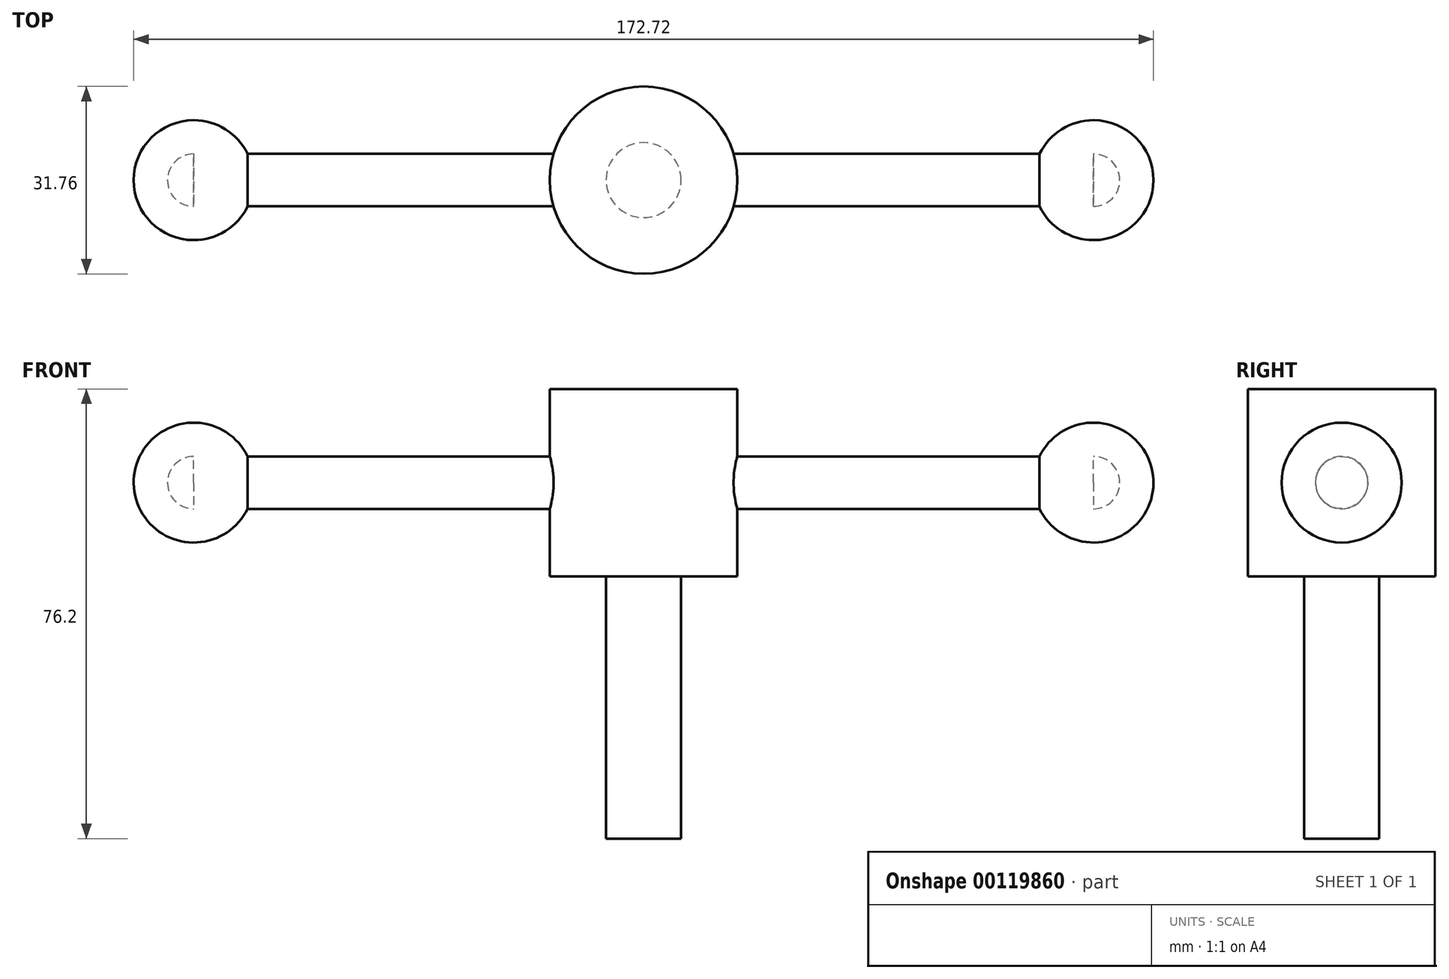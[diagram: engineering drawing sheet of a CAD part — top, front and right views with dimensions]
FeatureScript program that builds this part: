
annotation { "Feature Type Name" : "Feature", "Feature Type Description" : "" }
export const myFeature = defineFeature(function(context is Context, id is Id, definition is map)
    precondition{}
    {
        {
            var Q0;
            Q0=qCreatedBy(makeId("Top.planeOp"),FACE);
            var sketch = newSketch(context, id + "F0", { "sketchPlane" : qUnion([Q0])});
            skCircle(sketch, "E0", {"center": v(0, 0) * mm, "radius": 15.88 * mm});
            skCircle(sketch, "E1", {"center": v(0, 0) * mm, "radius": 6.35 * mm});
            skSolve(sketch);
        }
        {
            var Q0;
            Q0=makeQuery(id+"F0.imprint","IMPRINT",FACE,{"disambiguationData":[TD([[makeQuery(id+"F0.imprint","IMPRINT",EDGE,{"derivedFrom":sQuery(id+"F0.wireOp",EDGE,"E0")}),1.0]])]});
            extrude(context, id + "F1", {"entities" : qUnion([Q0]), "depth" : 31.75 * mm});
        }
        {
            var Q0;
            Q0=makeQuery(id+"F0.imprint","IMPRINT",FACE,{"disambiguationData":[TD([[makeQuery(id+"F0.imprint","IMPRINT",EDGE,{"derivedFrom":sQuery(id+"F0.wireOp",EDGE,"E1")}),1.0]])]});
            extrude(context, id + "F2", {"entities" : qUnion([Q0]), "operationType" : NewBodyOperationType.ADD, "depth" : 31.75 * mm, "hasSecondDirection" : true, "secondDirectionOppositeDirection" : true, "secondDirectionDepth" : 44.45 * mm});
        }
        {
            var Q0;
            Q0=qCreatedBy(makeId("Right.planeOp"),FACE);
            var sketch = newSketch(context, id + "F3", { "sketchPlane" : qUnion([Q0])});
            skLineSegment(sketch, "E2", {"start": v(0, 30.86) * mm, "end": v(0, 0) * mm, "construction": true});
            skLineSegment(sketch, "E3", {"start": v(0, 15.88) * mm, "end": v(-13.68, 15.88) * mm, "construction": true});
            skCircle(sketch, "E4", {"center": v(0, 15.88) * mm, "radius": 4.45 * mm});
            skSolve(sketch);
        }
        {
            var Q0;
            Q0 = qSketchRegion(id + "F3", true);
            extrude(context, id + "F4", {"entities" : qUnion([Q0]), "operationType" : NewBodyOperationType.ADD, "depth" : 76.2 * mm, "hasSecondDirection" : true, "secondDirectionOppositeDirection" : true, "secondDirectionDepth" : 76.2 * mm});
        }
        {
            var Q0;
            Q0=makeQuery(id+"F4.opExtrude","CAP_FACE",FACE,{"disambiguationData":[OSD([sQuery(id+"F3.wireOp",EDGE,"E4")])],"isStart":false});
            var sketch = newSketch(context, id + "F5", { "sketchPlane" : qUnion([Q0])});
            skCircle(sketch, "E5", {"center": v(0, 15.88) * mm, "radius": 10.16 * mm});
            skLineSegment(sketch, "E6", {"start": v(-10.16, 15.88) * mm, "end": v(10.16, 15.88) * mm});
            skSolve(sketch);
        }
        {
            var Q0;
            {var subQ0=sQuery(id+"F5.wireOp",EDGE,"E6");var subQ1=sQuery(id+"F5.wireOp",EDGE,"E5");var subQ2=makeQuery(id+"F5.imprint","INTERSECT",VERTEX,{"disambiguationData":[OD(0.0)],"derivedFrom":[subQ1,subQ0]});Q0=makeQuery(id+"F5.imprint","IMPRINT",FACE,{"disambiguationData":[TD([[makeQuery(id+"F5.imprint","IMPRINT",EDGE,{"disambiguationData":[TD([[subQ2,-1.0]])],"derivedFrom":subQ1}),1.0]])]});}
            var Q1;
            {var subQ0=sQuery(id+"F5.wireOp",EDGE,"E6");var subQ1=makeQuery(id+"F4.opExtrude","CAP_EDGE",EDGE,{"disambiguationData":[OSD([sQuery(id+"F3.wireOp",EDGE,"E4")])],"isStart":false});var subQ2=makeQuery(id+"F5.imprint","INTERSECT",VERTEX,{"disambiguationData":[OD(0.0)],"derivedFrom":[subQ1,subQ0]});Q1=makeQuery(id+"F5.imprint","IMPRINT",FACE,{"disambiguationData":[TD([[makeQuery(id+"F5.imprint","IMPRINT",EDGE,{"disambiguationData":[TD([[subQ2,-1.0]])],"derivedFrom":subQ0}),1.0]])]});}
            var Q2;
            {var subQ0=sQuery(id+"F5.wireOp",EDGE,"E6");var subQ1=makeQuery(id+"F4.opExtrude","CAP_EDGE",EDGE,{"disambiguationData":[OSD([sQuery(id+"F3.wireOp",EDGE,"E4")])],"isStart":false});var subQ2=makeQuery(id+"F5.imprint","INTERSECT",VERTEX,{"disambiguationData":[OD(0.0)],"derivedFrom":[subQ1,subQ0]});Q2=makeQuery(id+"F5.imprint","IMPRINT",FACE,{"disambiguationData":[TD([[makeQuery(id+"F5.imprint","IMPRINT",EDGE,{"disambiguationData":[TD([[subQ2,-1.0]])],"derivedFrom":subQ0}),-1.0]])]});}
            var Q3;
            Q3=sQuery(id+"F5.wireOp",EDGE,"E6");
            revolve(context, id + "F6", {"operationType" : NewBodyOperationType.ADD, "entities" : qUnion([Q0, Q1, Q2]), "axis" : qUnion([Q3]), "revolveType" : RevolveType.FULL});
        }
        {
            var Q0;
            Q0=makeQuery(id+"F4.opExtrude","CAP_FACE",FACE,{"disambiguationData":[OSD([sQuery(id+"F3.wireOp",EDGE,"E4")])],"isStart":true});
            var sketch = newSketch(context, id + "F7", { "sketchPlane" : qUnion([Q0])});
            skCircle(sketch, "E7", {"center": v(0, 15.88) * mm, "radius": 10.16 * mm});
            skLineSegment(sketch, "E8", {"start": v(-10.16, 15.88) * mm, "end": v(10.16, 15.88) * mm});
            skSolve(sketch);
        }
        {
            var Q0;
            {var subQ0=sQuery(id+"F7.wireOp",EDGE,"E8");var subQ1=sQuery(id+"F7.wireOp",EDGE,"E7");var subQ2=makeQuery(id+"F7.imprint","INTERSECT",VERTEX,{"disambiguationData":[OD(0.0)],"derivedFrom":[subQ1,subQ0]});Q0=makeQuery(id+"F7.imprint","IMPRINT",FACE,{"disambiguationData":[TD([[makeQuery(id+"F7.imprint","IMPRINT",EDGE,{"disambiguationData":[TD([[subQ2,-1.0]])],"derivedFrom":subQ1}),1.0]])]});}
            var Q1;
            {var subQ0=sQuery(id+"F7.wireOp",EDGE,"E8");var subQ1=makeQuery(id+"F4.opExtrude","CAP_EDGE",EDGE,{"disambiguationData":[OSD([sQuery(id+"F3.wireOp",EDGE,"E4")])],"isStart":true});var subQ2=makeQuery(id+"F7.imprint","INTERSECT",VERTEX,{"disambiguationData":[OD(0.0)],"derivedFrom":[subQ1,subQ0]});Q1=makeQuery(id+"F7.imprint","IMPRINT",FACE,{"disambiguationData":[TD([[makeQuery(id+"F7.imprint","IMPRINT",EDGE,{"disambiguationData":[TD([[subQ2,-1.0]])],"derivedFrom":subQ0}),1.0]])]});}
            var Q2;
            {var subQ0=sQuery(id+"F7.wireOp",EDGE,"E8");var subQ1=makeQuery(id+"F4.opExtrude","CAP_EDGE",EDGE,{"disambiguationData":[OSD([sQuery(id+"F3.wireOp",EDGE,"E4")])],"isStart":true});var subQ2=makeQuery(id+"F7.imprint","INTERSECT",VERTEX,{"disambiguationData":[OD(0.0)],"derivedFrom":[subQ1,subQ0]});Q2=makeQuery(id+"F7.imprint","IMPRINT",FACE,{"disambiguationData":[TD([[makeQuery(id+"F7.imprint","IMPRINT",EDGE,{"disambiguationData":[TD([[subQ2,-1.0]])],"derivedFrom":subQ0}),-1.0]])]});}
            var Q3;
            Q3=sQuery(id+"F7.wireOp",EDGE,"E8");
            revolve(context, id + "F8", {"operationType" : NewBodyOperationType.ADD, "entities" : qUnion([Q0, Q1, Q2]), "axis" : qUnion([Q3]), "revolveType" : RevolveType.FULL});
        }
    });
